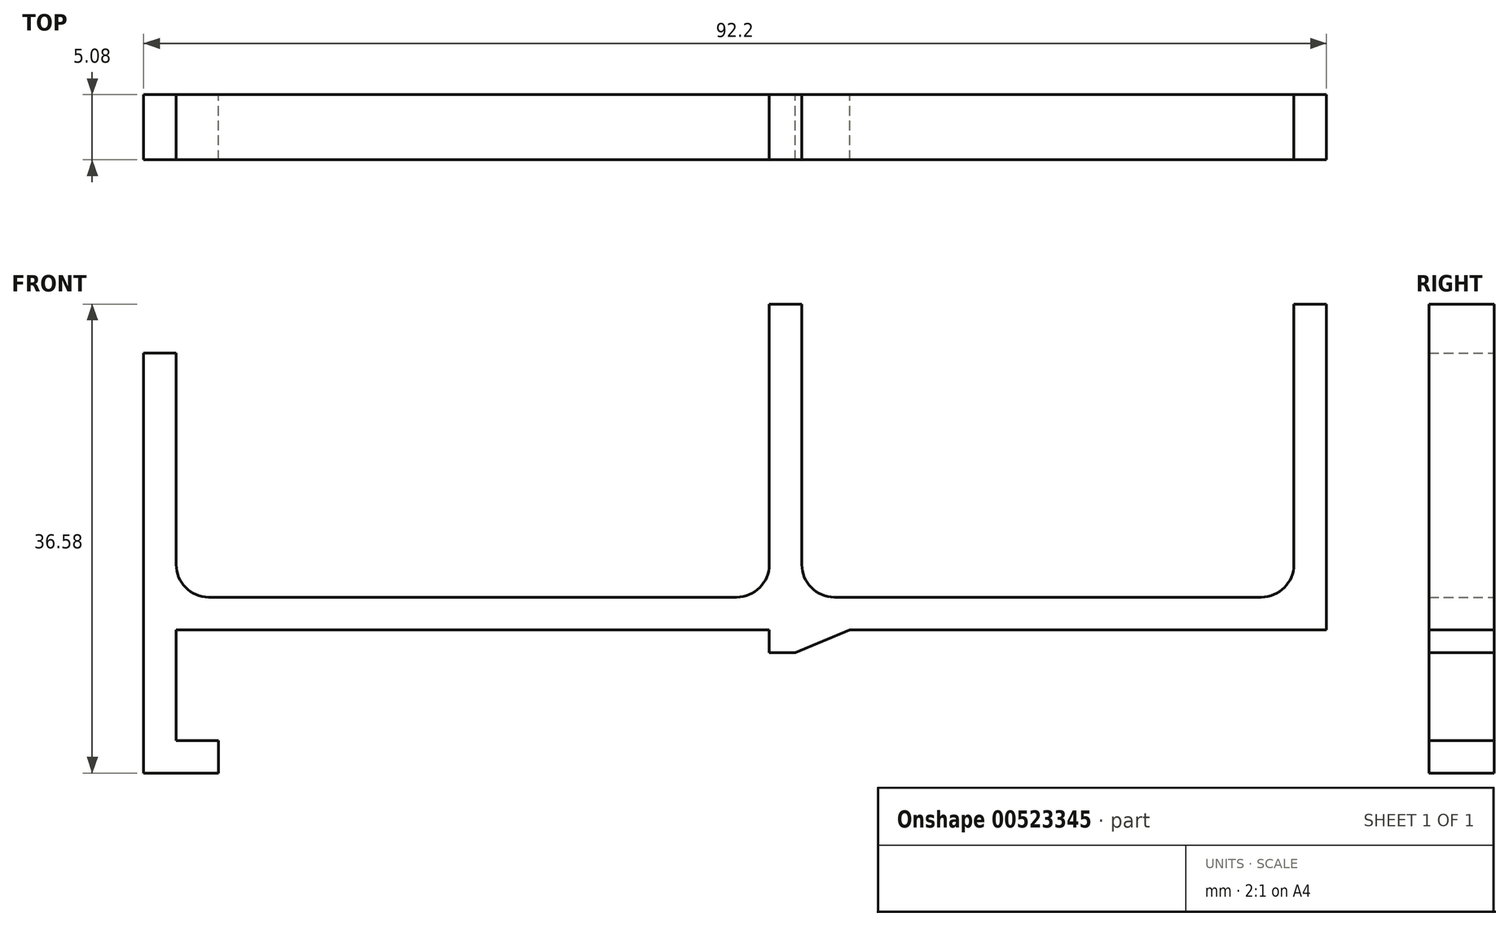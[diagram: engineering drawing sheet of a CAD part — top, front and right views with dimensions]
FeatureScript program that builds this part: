
annotation { "Feature Type Name" : "Feature", "Feature Type Description" : "" }
export const myFeature = defineFeature(function(context is Context, id is Id, definition is map)
    precondition{}
    {
        {
            var Q0;
            Q0=qCreatedBy(makeId("Front.planeOp"),FACE);
            var sketch = newSketch(context, id + "F0", { "sketchPlane" : qUnion([Q0])});
            skLineSegment(sketch, "E0", {"start": v(-23.11, 12.7) * mm, "end": v(23.11, 12.7) * mm});
            skLineSegment(sketch, "E1", {"start": v(23.11, 12.7) * mm, "end": v(23.11, 10.92) * mm});
            skLineSegment(sketch, "E2", {"start": v(-23.11, 12.7) * mm, "end": v(-23.11, 4.06) * mm});
            skLineSegment(sketch, "E3", {"start": v(-23.11, 4.06) * mm, "end": v(-19.81, 4.06) * mm});
            skLineSegment(sketch, "E4", {"start": v(-19.81, 4.06) * mm, "end": v(-19.81, 1.52) * mm});
            skLineSegment(sketch, "E5", {"start": v(-19.81, 1.52) * mm, "end": v(-25.65, 1.52) * mm});
            skLineSegment(sketch, "E6", {"start": v(-25.65, 1.52) * mm, "end": v(-25.65, 15.24) * mm});
            skLineSegment(sketch, "E7", {"start": v(-20.57, 15.24) * mm, "end": v(20.57, 15.24) * mm});
            skLineSegment(sketch, "E8", {"start": v(23.11, 10.92) * mm, "end": v(25.15, 10.92) * mm});
            skLineSegment(sketch, "E9", {"start": v(25.15, 10.92) * mm, "end": v(29.4, 12.7) * mm});
            skLineSegment(sketch, "E10", {"start": v(29.4, 12.7) * mm, "end": v(66.55, 12.7) * mm});
            skLineSegment(sketch, "E11", {"start": v(66.55, 12.7) * mm, "end": v(66.55, 38.1) * mm});
            skLineSegment(sketch, "E12", {"start": v(66.55, 38.1) * mm, "end": v(64, 38.1) * mm});
            skLineSegment(sketch, "E13", {"start": v(64, 38.1) * mm, "end": v(64, 17.78) * mm});
            skLineSegment(sketch, "E14", {"start": v(61.47, 15.24) * mm, "end": v(28.2, 15.24) * mm});
            skLineSegment(sketch, "E15", {"start": v(25.65, 17.78) * mm, "end": v(25.65, 38.1) * mm});
            skLineSegment(sketch, "E16", {"start": v(25.65, 38.1) * mm, "end": v(23.11, 38.1) * mm});
            skLineSegment(sketch, "E17", {"start": v(23.11, 38.1) * mm, "end": v(23.11, 17.78) * mm});
            skLineSegment(sketch, "E18", {"start": v(-25.65, 15.24) * mm, "end": v(-25.65, 34.3) * mm});
            skLineSegment(sketch, "E19", {"start": v(-25.65, 34.3) * mm, "end": v(-23.11, 34.3) * mm});
            skLineSegment(sketch, "E20", {"start": v(-23.11, 34.3) * mm, "end": v(-23.11, 17.78) * mm});
            skPoint(sketch, "E21.visualSharp", {"position": v(25.65, 15.24) * mm});
            skArc(sketch, "E21.filletArc", {"start": v(25.65, 17.78) * mm, "mid": v(26.4, 15.98) * mm, "end": v(28.2, 15.24) * mm});
            skPoint(sketch, "E22.visualSharp", {"position": v(64, 15.24) * mm});
            skArc(sketch, "E22.filletArc", {"start": v(61.47, 15.24) * mm, "mid": v(63.26, 15.98) * mm, "end": v(64, 17.78) * mm});
            skPoint(sketch, "E23.visualSharp", {"position": v(23.11, 15.24) * mm});
            skArc(sketch, "E23.filletArc", {"start": v(20.57, 15.24) * mm, "mid": v(22.37, 15.98) * mm, "end": v(23.11, 17.78) * mm});
            skPoint(sketch, "E24.visualSharp", {"position": v(-23.11, 15.24) * mm});
            skArc(sketch, "E24.filletArc", {"start": v(-23.11, 17.78) * mm, "mid": v(-22.37, 15.98) * mm, "end": v(-20.57, 15.24) * mm});
            skSolve(sketch);
        }
        {
            var Q0;
            Q0 = qSketchRegion(id + "F0", true);
            extrude(context, id + "F1", {"entities" : qUnion([Q0]), "depth" : 5.08 * mm, "offsetDistance" : 25.4 * mm});
        }
    });
